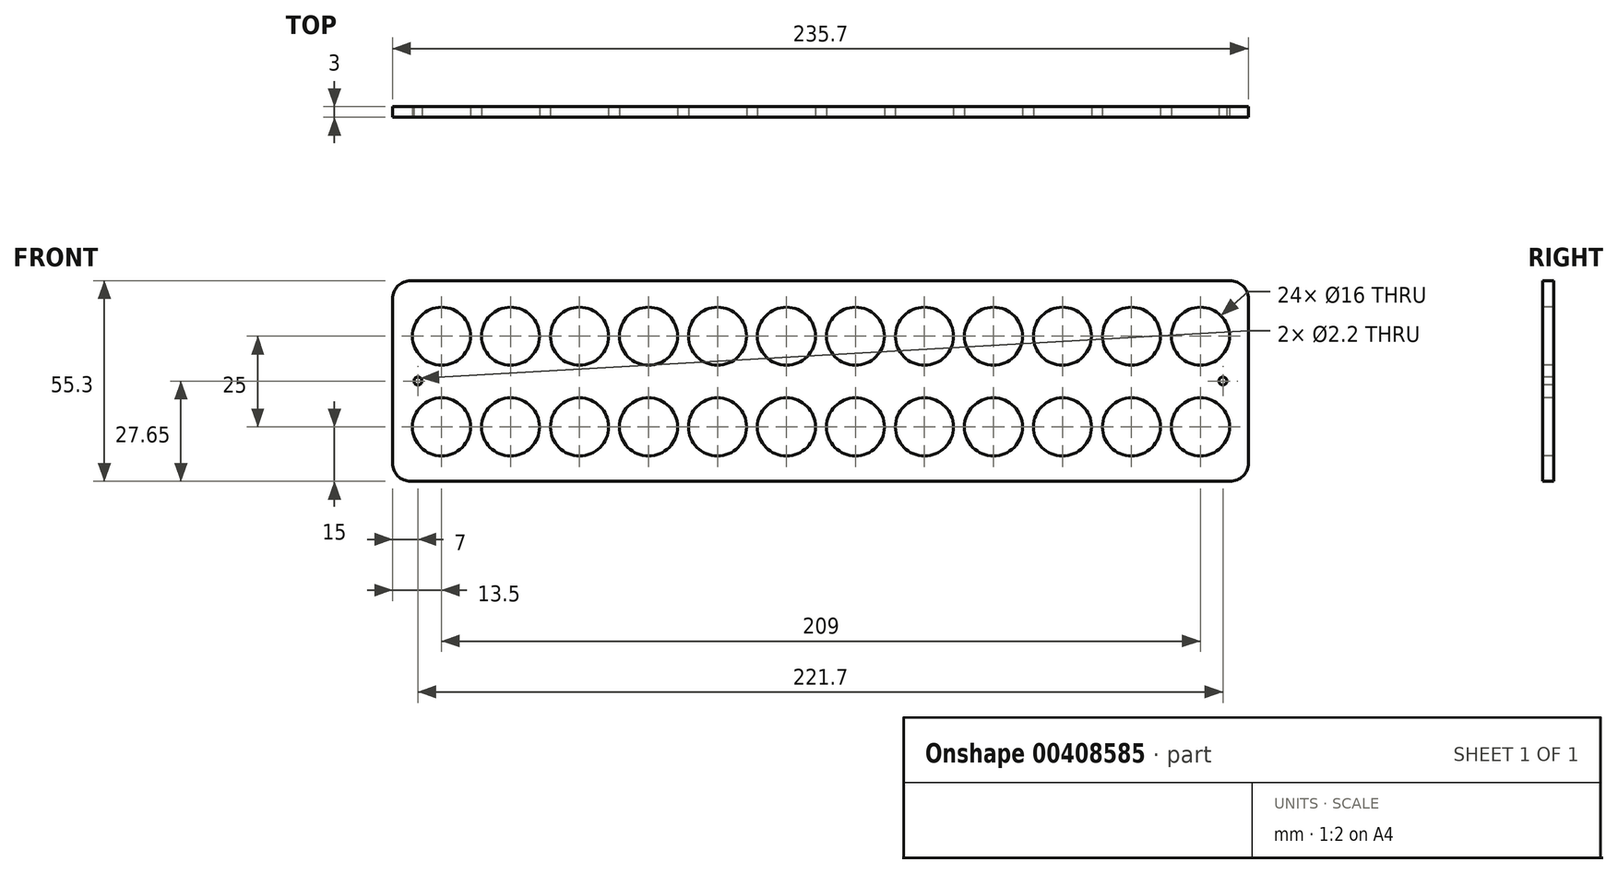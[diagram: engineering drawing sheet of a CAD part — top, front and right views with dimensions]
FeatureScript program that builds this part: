
annotation { "Feature Type Name" : "Feature", "Feature Type Description" : "" }
export const myFeature = defineFeature(function(context is Context, id is Id, definition is map)
    precondition{}
    {
        {
            var Q0;
            Q0=qCreatedBy(makeId("Front.planeOp"),FACE);
            var sketch = newSketch(context, id + "F0", { "sketchPlane" : qUnion([Q0])});
            skLineSegment(sketch, "E0.bottom", {"start": v(5, 0) * mm, "end": v(230.7, 0) * mm});
            skLineSegment(sketch, "E0.top", {"start": v(5, 55.3) * mm, "end": v(230.7, 55.3) * mm});
            skLineSegment(sketch, "E0.left", {"start": v(0, 5) * mm, "end": v(0, 50.3) * mm});
            skLineSegment(sketch, "E0.right", {"start": v(235.7, 5) * mm, "end": v(235.7, 50.3) * mm});
            skPoint(sketch, "E1.visualSharp", {"position": v(0, 55.3) * mm});
            skArc(sketch, "E1.filletArc", {"start": v(5, 55.3) * mm, "mid": v(1.46, 53.84) * mm, "end": v(0, 50.3) * mm});
            skPoint(sketch, "E2.visualSharp", {"position": v(0, 0) * mm});
            skArc(sketch, "E2.filletArc", {"start": v(0, 5) * mm, "mid": v(1.46, 1.46) * mm, "end": v(5, 0) * mm});
            skPoint(sketch, "E3.visualSharp", {"position": v(235.7, 0) * mm});
            skArc(sketch, "E3.filletArc", {"start": v(230.7, 0) * mm, "mid": v(234.24, 1.46) * mm, "end": v(235.7, 5) * mm});
            skPoint(sketch, "E4.visualSharp", {"position": v(235.7, 55.3) * mm});
            skArc(sketch, "E4.filletArc", {"start": v(235.7, 50.3) * mm, "mid": v(234.24, 53.84) * mm, "end": v(230.7, 55.3) * mm});
            skSolve(sketch);
        }
        {
            var Q0;
            Q0 = qSketchRegion(id + "F0", true);
            extrude(context, id + "F1", {"entities" : qUnion([Q0]), "depth" : 3 * mm});
        }
        {
            var Q0;
            Q0=makeQuery(id+"F1.opExtrude","CAP_FACE",FACE,{"disambiguationData":[OSD([sQuery(id+"F0.wireOp",EDGE,"E0.bottom"),sQuery(id+"F0.wireOp",EDGE,"E0.top"),sQuery(id+"F0.wireOp",EDGE,"E0.left"),sQuery(id+"F0.wireOp",EDGE,"E0.right"),sQuery(id+"F0.wireOp",EDGE,"E1.filletArc"),sQuery(id+"F0.wireOp",EDGE,"E2.filletArc"),sQuery(id+"F0.wireOp",EDGE,"E3.filletArc"),sQuery(id+"F0.wireOp",EDGE,"E4.filletArc")])],"isStart":false});
            var sketch = newSketch(context, id + "F2", { "sketchPlane" : qUnion([Q0])});
            skCircle(sketch, "E5", {"center": v(13.5, 15) * mm, "radius": 8 * mm});
            skCircle(sketch, "E6.0.1.0", {"center": v(13.5, 40) * mm, "radius": 8 * mm});
            skCircle(sketch, "E6.1.0.0", {"center": v(32.5, 15) * mm, "radius": 8 * mm});
            skCircle(sketch, "E6.1.1.0", {"center": v(32.5, 40) * mm, "radius": 8 * mm});
            skCircle(sketch, "E6.2.0.0", {"center": v(51.5, 15) * mm, "radius": 8 * mm});
            skCircle(sketch, "E6.2.1.0", {"center": v(51.5, 40) * mm, "radius": 8 * mm});
            skCircle(sketch, "E6.3.0.0", {"center": v(70.5, 15) * mm, "radius": 8 * mm});
            skCircle(sketch, "E6.3.1.0", {"center": v(70.5, 40) * mm, "radius": 8 * mm});
            skCircle(sketch, "E6.4.0.0", {"center": v(89.5, 15) * mm, "radius": 8 * mm});
            skCircle(sketch, "E6.4.1.0", {"center": v(89.5, 40) * mm, "radius": 8 * mm});
            skCircle(sketch, "E6.5.0.0", {"center": v(108.5, 15) * mm, "radius": 8 * mm});
            skCircle(sketch, "E6.5.1.0", {"center": v(108.5, 40) * mm, "radius": 8 * mm});
            skCircle(sketch, "E6.6.0.0", {"center": v(127.5, 15) * mm, "radius": 8 * mm});
            skCircle(sketch, "E6.6.1.0", {"center": v(127.5, 40) * mm, "radius": 8 * mm});
            skCircle(sketch, "E6.7.0.0", {"center": v(146.5, 15) * mm, "radius": 8 * mm});
            skCircle(sketch, "E6.7.1.0", {"center": v(146.5, 40) * mm, "radius": 8 * mm});
            skCircle(sketch, "E6.8.0.0", {"center": v(165.5, 15) * mm, "radius": 8 * mm});
            skCircle(sketch, "E6.8.1.0", {"center": v(165.5, 40) * mm, "radius": 8 * mm});
            skCircle(sketch, "E6.9.0.0", {"center": v(184.5, 15) * mm, "radius": 8 * mm});
            skCircle(sketch, "E6.9.1.0", {"center": v(184.5, 40) * mm, "radius": 8 * mm});
            skCircle(sketch, "E6.10.0.0", {"center": v(203.5, 15) * mm, "radius": 8 * mm});
            skCircle(sketch, "E6.10.1.0", {"center": v(203.5, 40) * mm, "radius": 8 * mm});
            skCircle(sketch, "E6.11.0.0", {"center": v(222.5, 15) * mm, "radius": 8 * mm});
            skCircle(sketch, "E6.11.1.0", {"center": v(222.5, 40) * mm, "radius": 8 * mm});
            skLineSegment(sketch, "E6.direction1", {"start": v(13.5, 15) * mm, "end": v(32.5, 15) * mm, "construction": true});
            skLineSegment(sketch, "E6.direction2", {"start": v(13.5, 15) * mm, "end": v(13.5, 40) * mm, "construction": true});
            skCircle(sketch, "E7", {"center": v(7, 27.65) * mm, "radius": 1.1 * mm});
            skPoint(sketch, "E7.centerSnap0", {"position": v(0, 27.65) * mm});
            skCircle(sketch, "E8", {"center": v(228.7, 27.65) * mm, "radius": 1.1 * mm});
            skSolve(sketch);
        }
        {
            var Q0;
            Q0 = qSketchRegion(id + "F2", true);
            extrude(context, id + "F3", {"entities" : qUnion([Q0]), "operationType" : NewBodyOperationType.REMOVE, "oppositeDirection" : true, "depth" : 25 * mm});
        }
    });
